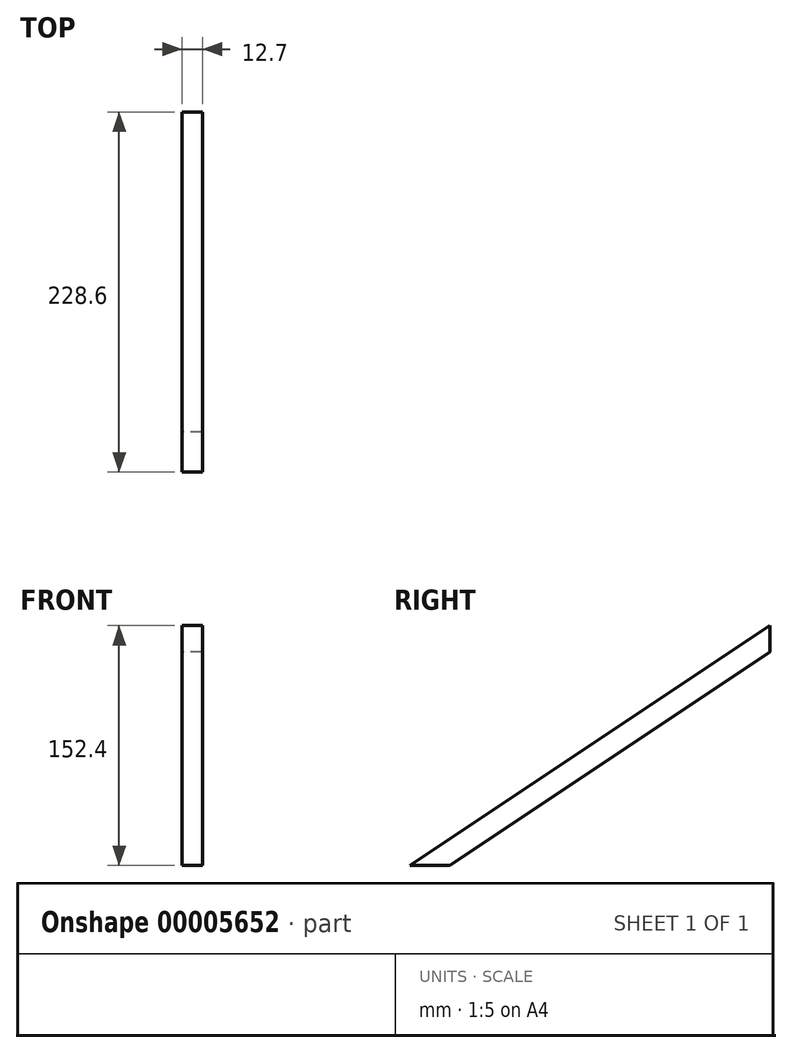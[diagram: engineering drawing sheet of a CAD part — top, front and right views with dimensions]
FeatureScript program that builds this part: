
annotation { "Feature Type Name" : "Feature", "Feature Type Description" : "" }
export const myFeature = defineFeature(function(context is Context, id is Id, definition is map)
    precondition{}
    {
        {
            var Q0;
            Q0=qCreatedBy(makeId("Right.planeOp"),FACE);
            var sketch = newSketch(context, id + "F0", { "sketchPlane" : qUnion([Q0])});
            skLineSegment(sketch, "E0", {"start": v(0, 0) * mm, "end": v(228.6, 152.4) * mm});
            skLineSegment(sketch, "E1", {"start": v(228.6, 152.4) * mm, "end": v(228.6, 135.47) * mm});
            skLineSegment(sketch, "E2", {"start": v(228.6, 135.47) * mm, "end": v(25.4, 0) * mm});
            skLineSegment(sketch, "E3", {"start": v(25.4, 0) * mm, "end": v(0, 0) * mm});
            skLineSegment(sketch, "E4", {"start": v(0, 0) * mm, "end": v(0, -457.2) * mm, "construction": true});
            skLineSegment(sketch, "E5", {"start": v(0, -457.2) * mm, "end": v(660.4, -457.2) * mm, "construction": true});
            skLineSegment(sketch, "E6", {"start": v(660.4, -457.2) * mm, "end": v(660.4, 152.4) * mm, "construction": true});
            skLineSegment(sketch, "E7", {"start": v(660.4, 152.4) * mm, "end": v(228.6, 152.4) * mm, "construction": true});
            skSolve(sketch);
        }
        {
            var Q0;
            Q0 = qSketchRegion(id + "F0", true);
            extrude(context, id + "F1", {"entities" : qUnion([Q0]), "depth" : 12.7 * mm});
        }
        {
            var Q0;
            Q0=makeQuery(id+"F1.opExtrude","SWEPT_FACE",FACE,{"disambiguationData":[OSD([sQuery(id+"F0.wireOp",EDGE,"E0")])]});
            var sketch = newSketch(context, id + "F2", { "sketchPlane" : qUnion([Q0])});
            skLineSegment(sketch, "E8", {"start": v(3.17, 274.74) * mm, "end": v(3.18, 0) * mm});
            skLineSegment(sketch, "E9", {"start": v(3.18, 0) * mm, "end": v(9.52, 0) * mm});
            skLineSegment(sketch, "E10", {"start": v(9.52, 0) * mm, "end": v(9.52, 274.74) * mm});
            skLineSegment(sketch, "E11", {"start": v(9.52, 274.74) * mm, "end": v(3.17, 274.74) * mm});
            skSolve(sketch);
        }
        {
            var Q0;
            Q0 = qSketchRegion(id + "F2", true);
            extrude(context, id + "F3", {"entities" : qUnion([Q0]), "depth" : 3.17 * mm});
        }
        {
            var Q0;
            Q0=makeQuery(id+"F3.opExtrude","CAP_FACE",FACE,{"disambiguationData":[OSD([sQuery(id+"F2.wireOp",EDGE,"E8"),sQuery(id+"F2.wireOp",EDGE,"E9"),sQuery(id+"F2.wireOp",EDGE,"E10"),sQuery(id+"F2.wireOp",EDGE,"E11")])],"isStart":false});
            fillet(context, id + "F4", {"entities" : qUnion([Q0]), "radius" : 2.54 * mm, "tangentPropagation" : true, "allowEdgeOverflow" : false});
        }
        {
            var Q0;
            Q0=makeQuery(id+"F3.opExtrude","SWEPT_BODY",BODY,{"disambiguationData":[OSD([sQuery(id+"F2.wireOp",EDGE,"E8"),sQuery(id+"F2.wireOp",EDGE,"E9"),sQuery(id+"F2.wireOp",EDGE,"E10"),sQuery(id+"F2.wireOp",EDGE,"E11")])]});
            deleteBodies(context, id + "F5", {"entities" : qUnion([Q0])});
        }
    });
